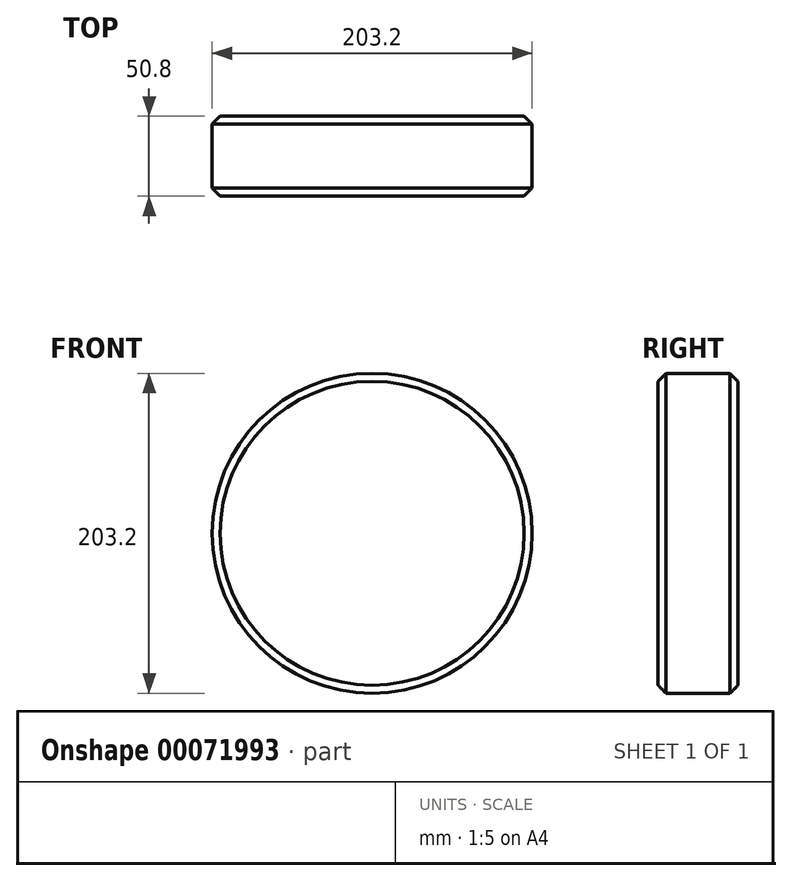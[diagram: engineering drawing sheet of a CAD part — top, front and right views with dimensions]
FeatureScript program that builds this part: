
annotation { "Feature Type Name" : "Feature", "Feature Type Description" : "" }
export const myFeature = defineFeature(function(context is Context, id is Id, definition is map)
    precondition{}
    {
        {
            var Q0;
            Q0=qCreatedBy(makeId("Front.planeOp"),FACE);
            var sketch = newSketch(context, id + "F0", { "sketchPlane" : qUnion([Q0])});
            skCircle(sketch, "E0", {"center": v(0, 0) * mm, "radius": 101.6 * mm});
            skSolve(sketch);
        }
        {
            var Q0;
            Q0=makeQuery(id+"F0.imprint","IMPRINT",FACE,{"disambiguationData":[TD([[makeQuery(id+"F0.imprint","IMPRINT",EDGE,{"derivedFrom":sQuery(id+"F0.wireOp",EDGE,"E0")}),1.0]])]});
            extrude(context, id + "F1", {"entities" : qUnion([Q0]), "depth" : 50.8 * mm});
        }
        {
            var Q0;
            Q0=makeQuery(id+"F1.opExtrude","CAP_FACE",FACE,{"disambiguationData":[OSD([sQuery(id+"F0.wireOp",EDGE,"E0")])],"isStart":true});
            var Q1;
            Q1=makeQuery(id+"F1.opExtrude","SWEPT_FACE",FACE,{"disambiguationData":[OSD([sQuery(id+"F0.wireOp",EDGE,"E0")])]});
            chamfer(context, id + "F2", {"entities" : qUnion([Q0, Q1]), "width" : 5.08 * mm, "tangentPropagation" : true});
        }
    });
